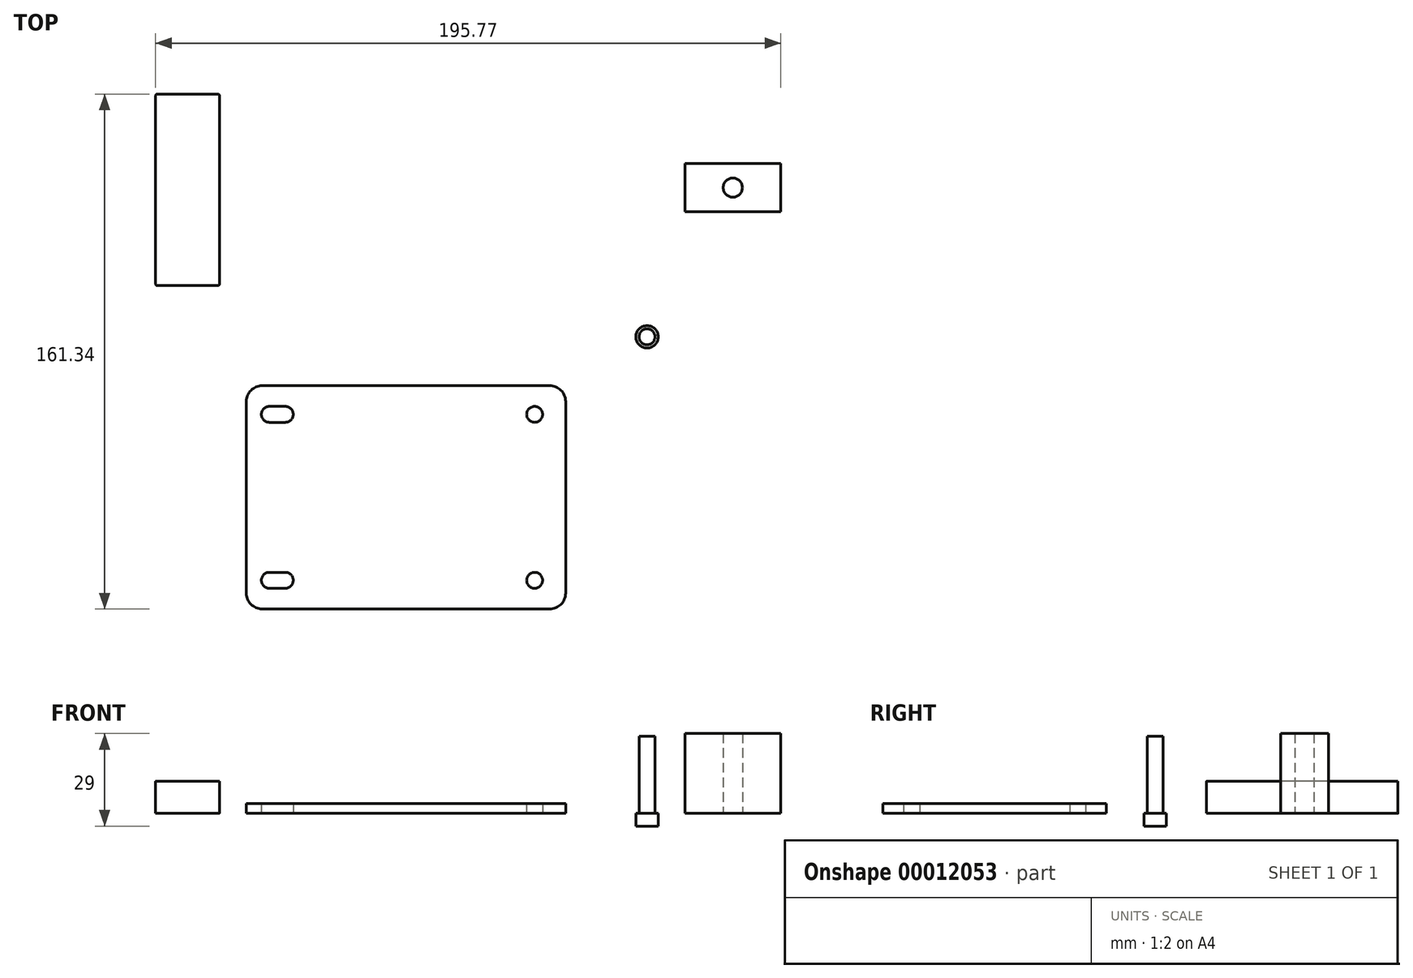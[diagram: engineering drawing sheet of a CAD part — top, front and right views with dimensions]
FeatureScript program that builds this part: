
annotation { "Feature Type Name" : "Feature", "Feature Type Description" : "" }
export const myFeature = defineFeature(function(context is Context, id is Id, definition is map)
    precondition{}
    {
        {
            var Q0;
            Q0=qCreatedBy(makeId("Top.planeOp"),FACE);
            var sketch = newSketch(context, id + "F0", { "sketchPlane" : qUnion([Q0])});
            skCircle(sketch, "E0", {"center": v(0, 0) * mm, "radius": 2.5 * mm});
            skCircle(sketch, "E1", {"center": v(0, 0) * mm, "radius": 3.5 * mm});
            skSolve(sketch);
        }
        {
            var Q0;
            Q0=makeQuery(id+"F0.imprint","IMPRINT",FACE,{"disambiguationData":[TD([[makeQuery(id+"F0.imprint","IMPRINT",EDGE,{"derivedFrom":sQuery(id+"F0.wireOp",EDGE,"E0")}),1.0]])]});
            extrude(context, id + "F1", {"entities" : qUnion([Q0]), "depth" : 24.2 * mm});
        }
        {
            var Q0;
            Q0=makeQuery(id+"F0.imprint","IMPRINT",FACE,{"disambiguationData":[TD([[makeQuery(id+"F0.imprint","IMPRINT",EDGE,{"derivedFrom":sQuery(id+"F0.wireOp",EDGE,"E0")}),-1.0]])]});
            var Q1;
            Q1=makeQuery(id+"F0.imprint","IMPRINT",FACE,{"disambiguationData":[TD([[makeQuery(id+"F0.imprint","IMPRINT",EDGE,{"derivedFrom":sQuery(id+"F0.wireOp",EDGE,"E0")}),1.0]])]});
            extrude(context, id + "F2", {"entities" : qUnion([Q0, Q1]), "operationType" : NewBodyOperationType.ADD, "oppositeDirection" : true, "depth" : 4 * mm});
        }
        {
            var Q0;
            Q0=qCreatedBy(makeId("Top.planeOp"),FACE);
            var sketch = newSketch(context, id + "F3", { "sketchPlane" : qUnion([Q0])});
            skLineSegment(sketch, "E2.bottom", {"start": v(-125.5, -15.3) * mm, "end": v(-25.5, -15.3) * mm});
            skLineSegment(sketch, "E2.top", {"start": v(-125.5, -85.3) * mm, "end": v(-25.5, -85.3) * mm});
            skLineSegment(sketch, "E2.left", {"start": v(-125.5, -15.3) * mm, "end": v(-125.5, -85.3) * mm});
            skLineSegment(sketch, "E2.right", {"start": v(-25.5, -15.3) * mm, "end": v(-25.5, -85.3) * mm});
            skLineSegment(sketch, "E3", {"start": v(-75.5, -15.3) * mm, "end": v(-75.5, -85.3) * mm, "construction": true});
            skCircle(sketch, "E4", {"center": v(-115.8, -24.3) * mm, "radius": 2.5 * mm});
            skCircle(sketch, "E5", {"center": v(-115.8, -76.3) * mm, "radius": 2.5 * mm});
            skCircle(sketch, "E6.0.MirrorC", {"center": v(-35.2, -24.3) * mm, "radius": 2.5 * mm});
            skCircle(sketch, "E7.0.MirrorC", {"center": v(-35.2, -76.3) * mm, "radius": 2.5 * mm});
            skLineSegment(sketch, "E8", {"start": v(-115.8, -24.3) * mm, "end": v(-113.3, -24.3) * mm, "construction": true});
            skLineSegment(sketch, "E9", {"start": v(-115.8, -24.3) * mm, "end": v(-118.3, -24.3) * mm, "construction": true});
            skLineSegment(sketch, "E10", {"start": v(-115.8, -76.3) * mm, "end": v(-113.3, -76.3) * mm, "construction": true});
            skLineSegment(sketch, "E11", {"start": v(-115.8, -76.3) * mm, "end": v(-118.3, -76.3) * mm, "construction": true});
            skCircle(sketch, "E12", {"center": v(-118.3, -76.3) * mm, "radius": 2.5 * mm});
            skCircle(sketch, "E13", {"center": v(-113.3, -76.3) * mm, "radius": 2.5 * mm});
            skCircle(sketch, "E14", {"center": v(-113.3, -24.3) * mm, "radius": 2.5 * mm});
            skCircle(sketch, "E15", {"center": v(-118.3, -24.3) * mm, "radius": 2.5 * mm});
            skLineSegment(sketch, "E16", {"start": v(-120.85, -73.8) * mm, "end": v(-113.3, -73.8) * mm});
            skLineSegment(sketch, "E17", {"start": v(-120.85, -78.8) * mm, "end": v(-113.3, -78.8) * mm});
            skLineSegment(sketch, "E18", {"start": v(-118.3, -26.8) * mm, "end": v(-113.3, -26.8) * mm});
            skLineSegment(sketch, "E19", {"start": v(-113.3, -21.8) * mm, "end": v(-118.3, -21.8) * mm});
            skSolve(sketch);
        }
        {
            var Q0;
            Q0=makeQuery(id+"F3.imprint","IMPRINT",FACE,{"disambiguationData":[TD([[makeQuery(id+"F3.imprint","IMPRINT",EDGE,{"derivedFrom":sQuery(id+"F3.wireOp",EDGE,"E2.bottom")}),-1.0]])]});
            extrude(context, id + "F4", {"entities" : qUnion([Q0]), "depth" : 3 * mm});
        }
        {
            var Q0;
            Q0=makeQuery(id+"F4.opExtrude","SWEPT_EDGE",EDGE,{"disambiguationData":[OSD([sQuery(id+"F3.wireOp",EDGE,"E2.bottom"),sQuery(id+"F3.wireOp",EDGE,"E2.left")])]});
            var Q1;
            Q1=makeQuery(id+"F4.opExtrude","SWEPT_EDGE",EDGE,{"disambiguationData":[OSD([sQuery(id+"F3.wireOp",EDGE,"E2.bottom"),sQuery(id+"F3.wireOp",EDGE,"E2.right")])]});
            var Q2;
            Q2=makeQuery(id+"F4.opExtrude","SWEPT_EDGE",EDGE,{"disambiguationData":[OSD([sQuery(id+"F3.wireOp",EDGE,"E2.top"),sQuery(id+"F3.wireOp",EDGE,"E2.right")])]});
            var Q3;
            Q3=makeQuery(id+"F4.opExtrude","SWEPT_EDGE",EDGE,{"disambiguationData":[OSD([sQuery(id+"F3.wireOp",EDGE,"E2.top"),sQuery(id+"F3.wireOp",EDGE,"E2.left")])]});
            fillet(context, id + "F5", {"entities" : qUnion([Q0, Q1, Q2, Q3]), "radius" : 5 * mm, "tangentPropagation" : true, "allowEdgeOverflow" : false});
        }
        {
            var Q0;
            Q0=qCreatedBy(makeId("Top.planeOp"),FACE);
            var sketch = newSketch(context, id + "F6", { "sketchPlane" : qUnion([Q0])});
            skLineSegment(sketch, "E20.bottom", {"start": v(11.87, 54.24) * mm, "end": v(41.87, 54.24) * mm});
            skLineSegment(sketch, "E20.top", {"start": v(11.87, 39.24) * mm, "end": v(41.87, 39.24) * mm});
            skLineSegment(sketch, "E20.left", {"start": v(11.87, 54.24) * mm, "end": v(11.87, 39.24) * mm});
            skLineSegment(sketch, "E20.right", {"start": v(41.87, 54.24) * mm, "end": v(41.87, 39.24) * mm});
            skCircle(sketch, "E21", {"center": v(26.87, 46.74) * mm, "radius": 3 * mm});
            skSolve(sketch);
        }
        {
            var Q0;
            Q0 = qSketchRegion(id + "F6", true);
            extrude(context, id + "F7", {"entities" : qUnion([Q0]), "depth" : 25 * mm});
        }
        {
            var Q0;
            Q0=qCreatedBy(makeId("Top.planeOp"),FACE);
            var sketch = newSketch(context, id + "F8", { "sketchPlane" : qUnion([Q0])});
            skLineSegment(sketch, "E22.bottom", {"start": v(-153.4, 76.05) * mm, "end": v(-134.4, 76.05) * mm});
            skLineSegment(sketch, "E22.top", {"start": v(-153.4, 16.05) * mm, "end": v(-134.4, 16.05) * mm});
            skLineSegment(sketch, "E22.left", {"start": v(-153.9, 75.55) * mm, "end": v(-153.9, 16.55) * mm});
            skLineSegment(sketch, "E22.right", {"start": v(-133.9, 75.55) * mm, "end": v(-133.9, 16.55) * mm});
            skPoint(sketch, "E23.visualSharp", {"position": v(-153.9, 76.05) * mm});
            skArc(sketch, "E23.filletArc", {"start": v(-153.4, 76.05) * mm, "mid": v(-153.76, 75.9) * mm, "end": v(-153.9, 75.55) * mm});
            skPoint(sketch, "E24.visualSharp", {"position": v(-133.9, 76.05) * mm});
            skArc(sketch, "E24.filletArc", {"start": v(-133.9, 75.55) * mm, "mid": v(-134.05, 75.9) * mm, "end": v(-134.4, 76.05) * mm});
            skPoint(sketch, "E25.visualSharp", {"position": v(-133.9, 16.05) * mm});
            skArc(sketch, "E25.filletArc", {"start": v(-134.4, 16.05) * mm, "mid": v(-134.05, 16.2) * mm, "end": v(-133.9, 16.55) * mm});
            skPoint(sketch, "E26.visualSharp", {"position": v(-153.9, 16.05) * mm});
            skArc(sketch, "E26.filletArc", {"start": v(-153.9, 16.55) * mm, "mid": v(-153.76, 16.2) * mm, "end": v(-153.4, 16.05) * mm});
            skSolve(sketch);
        }
        {
            var Q0;
            Q0=makeQuery(id+"F8.imprint","IMPRINT",FACE,{"disambiguationData":[TD([[makeQuery(id+"F8.imprint","IMPRINT",EDGE,{"derivedFrom":sQuery(id+"F8.wireOp",EDGE,"E22.bottom")}),-1.0]])]});
            extrude(context, id + "F9", {"entities" : qUnion([Q0]), "depth" : 10 * mm});
        }
    });
